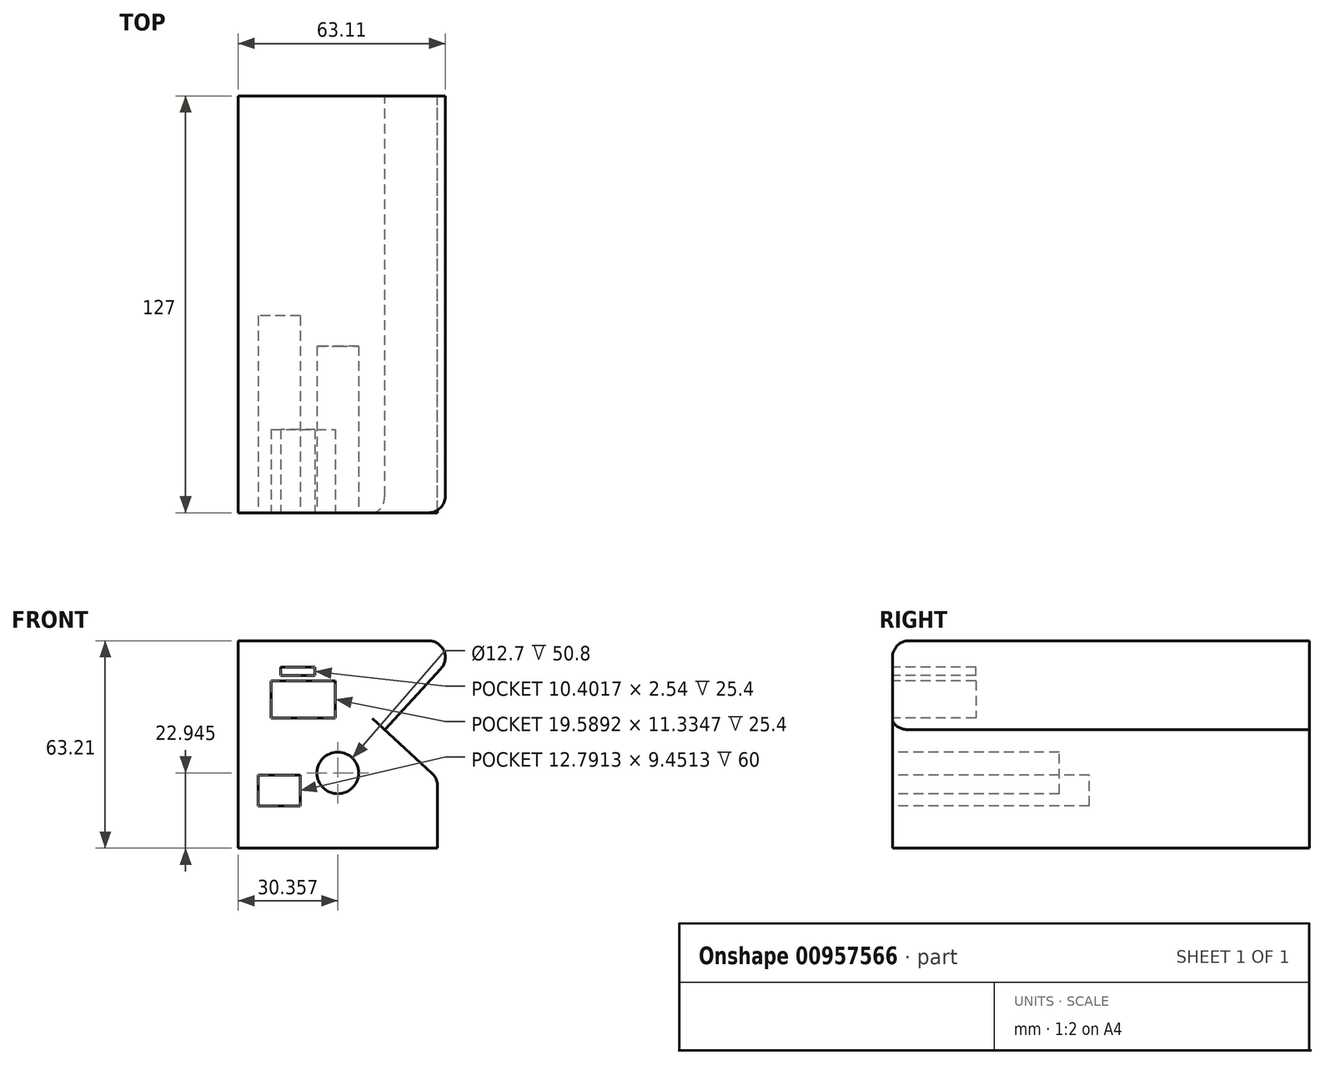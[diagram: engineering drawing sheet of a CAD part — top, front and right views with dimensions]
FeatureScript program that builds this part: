
annotation { "Feature Type Name" : "Feature", "Feature Type Description" : "" }
export const myFeature = defineFeature(function(context is Context, id is Id, definition is map)
    precondition{}
    {
        {
            var Q0;
            Q0=qCreatedBy(makeId("Front.planeOp"),FACE);
            var sketch = newSketch(context, id + "F0", { "sketchPlane" : qUnion([Q0])});
            skLineSegment(sketch, "E0", {"start": v(0, 0) * mm, "end": v(0, 63.21) * mm});
            skLineSegment(sketch, "E1", {"start": v(0, 63.21) * mm, "end": v(69.6, 63.21) * mm});
            skLineSegment(sketch, "E2", {"start": v(69.6, 63.21) * mm, "end": v(44.64, 36.06) * mm});
            skLineSegment(sketch, "E3", {"start": v(44.64, 36.06) * mm, "end": v(60.71, 21.29) * mm});
            skLineSegment(sketch, "E4", {"start": v(60.71, 21.29) * mm, "end": v(60.71, 0) * mm});
            skLineSegment(sketch, "E5", {"start": v(60.71, 0) * mm, "end": v(0, 0) * mm});
            skSolve(sketch);
        }
        {
            var Q0;
            Q0 = qSketchRegion(id + "F0", true);
            extrude(context, id + "F1", {"entities" : qUnion([Q0]), "depth" : 127 * mm, "offsetDistance" : 25.4 * mm});
        }
        {
            var Q0;
            Q0=makeQuery(id+"F1.opExtrude","SWEPT_EDGE",EDGE,{"disambiguationData":[OSD([sQuery(id+"F0.wireOp",EDGE,"E1"),sQuery(id+"F0.wireOp",EDGE,"E2")])]});
            var Q1;
            Q1=makeQuery(id+"F1.opExtrude","SWEPT_EDGE",EDGE,{"disambiguationData":[OSD([sQuery(id+"F0.wireOp",EDGE,"E3"),sQuery(id+"F0.wireOp",EDGE,"E4")])]});
            fillet(context, id + "F2", {"entities" : qUnion([Q0, Q1]), "radius" : 5.08 * mm, "tangentPropagation" : true, "allowEdgeOverflow" : false});
        }
        {
            var Q0;
            Q0=makeQuery(id+"F1.opExtrude","CAP_FACE",FACE,{"disambiguationData":[OSD([sQuery(id+"F0.wireOp",EDGE,"E0"),sQuery(id+"F0.wireOp",EDGE,"E1"),sQuery(id+"F0.wireOp",EDGE,"E2"),sQuery(id+"F0.wireOp",EDGE,"E3"),sQuery(id+"F0.wireOp",EDGE,"E4"),sQuery(id+"F0.wireOp",EDGE,"E5")])],"isStart":false});
            var sketch = newSketch(context, id + "F3", { "sketchPlane" : qUnion([Q0])});
            skCircle(sketch, "E6", {"center": v(30.36, 22.94) * mm, "radius": 6.35 * mm});
            skPoint(sketch, "E6.centerSnap0", {"position": v(30.36, 0) * mm});
            skSolve(sketch);
        }
        {
            var Q0;
            Q0=makeQuery(id+"F3.imprint","IMPRINT",FACE,{"disambiguationData":[TD([[makeQuery(id+"F3.imprint","IMPRINT",EDGE,{"derivedFrom":sQuery(id+"F3.wireOp",EDGE,"E6")}),1.0]])]});
            var Q1;
            Q1=sQuery(id+"F3.wireOp",EDGE,"E6");
            extrude(context, id + "F4", {"entities" : qUnion([Q0]), "operationType" : NewBodyOperationType.REMOVE, "surfaceEntities" : qUnion([Q1]), "oppositeDirection" : true, "depth" : 50.8 * mm, "offsetDistance" : 25.4 * mm});
        }
        {
            var Q0;
            Q0=makeQuery(id+"F1.opExtrude","CAP_FACE",FACE,{"disambiguationData":[OSD([sQuery(id+"F0.wireOp",EDGE,"E0"),sQuery(id+"F0.wireOp",EDGE,"E1"),sQuery(id+"F0.wireOp",EDGE,"E2"),sQuery(id+"F0.wireOp",EDGE,"E3"),sQuery(id+"F0.wireOp",EDGE,"E4"),sQuery(id+"F0.wireOp",EDGE,"E5")])],"isStart":false});
            var sketch = newSketch(context, id + "F5", { "sketchPlane" : qUnion([Q0])});
            skLineSegment(sketch, "E7.bottom", {"start": v(10.05, 51.03) * mm, "end": v(29.64, 51.03) * mm});
            skLineSegment(sketch, "E7.top", {"start": v(10.05, 39.7) * mm, "end": v(29.64, 39.7) * mm});
            skLineSegment(sketch, "E7.left", {"start": v(10.05, 51.03) * mm, "end": v(10.05, 39.7) * mm});
            skLineSegment(sketch, "E7.right", {"start": v(29.64, 51.03) * mm, "end": v(29.64, 39.7) * mm});
            skPoint(sketch, "E7.middle", {"position": v(19.85, 45.37) * mm});
            skSolve(sketch);
        }
        {
            var Q0;
            Q0=makeQuery(id+"F1.opExtrude","CAP_FACE",FACE,{"disambiguationData":[OSD([sQuery(id+"F0.wireOp",EDGE,"E0"),sQuery(id+"F0.wireOp",EDGE,"E1"),sQuery(id+"F0.wireOp",EDGE,"E2"),sQuery(id+"F0.wireOp",EDGE,"E3"),sQuery(id+"F0.wireOp",EDGE,"E4"),sQuery(id+"F0.wireOp",EDGE,"E5")])],"isStart":false});
            var sketch = newSketch(context, id + "F6", { "sketchPlane" : qUnion([Q0])});
            skLineSegment(sketch, "E8.bottom", {"start": v(23.4, 55.13) * mm, "end": v(13, 55.13) * mm});
            skLineSegment(sketch, "E8.top", {"start": v(23.4, 52.59) * mm, "end": v(13, 52.59) * mm});
            skLineSegment(sketch, "E8.left", {"start": v(23.4, 52.59) * mm, "end": v(23.4, 55.13) * mm});
            skLineSegment(sketch, "E8.right", {"start": v(13, 52.59) * mm, "end": v(13, 55.13) * mm});
            skPoint(sketch, "E8.middle", {"position": v(18.2, 53.86) * mm});
            skSolve(sketch);
        }
        {
            var Q0;
            Q0 = qSketchRegion(id + "F6", true);
            extrude(context, id + "F7", {"entities" : qUnion([Q0]), "operationType" : NewBodyOperationType.REMOVE, "oppositeDirection" : true, "depth" : 25.4 * mm, "offsetDistance" : 25.4 * mm});
        }
        {
            var Q0;
            Q0=makeQuery(id+"F5.imprint","IMPRINT",FACE,{"disambiguationData":[TD([[makeQuery(id+"F5.imprint","IMPRINT",EDGE,{"derivedFrom":sQuery(id+"F5.wireOp",EDGE,"E7.bottom")}),-1.0]])]});
            var Q1;
            Q1=sQuery(id+"F5.wireOp",EDGE,"E7.bottom");
            var Q2;
            Q2=sQuery(id+"F5.wireOp",EDGE,"E7.right");
            var Q3;
            Q3=sQuery(id+"F5.wireOp",EDGE,"E7.top");
            var Q4;
            Q4=sQuery(id+"F5.wireOp",EDGE,"E7.left");
            extrude(context, id + "F8", {"entities" : qUnion([Q0]), "operationType" : NewBodyOperationType.REMOVE, "surfaceEntities" : qUnion([Q1, Q2, Q3, Q4]), "oppositeDirection" : true, "depth" : 25.4 * mm, "offsetDistance" : 25.4 * mm});
        }
        {
            var Q0;
            Q0=makeQuery(id+"F1.opExtrude","CAP_EDGE",EDGE,{"disambiguationData":[OSD([sQuery(id+"F0.wireOp",EDGE,"E1")])],"isStart":false});
            fillet(context, id + "F9", {"entities" : qUnion([Q0]), "radius" : 5.08 * mm, "tangentPropagation" : true, "allowEdgeOverflow" : false});
        }
        {
            var Q0;
            Q0=makeQuery(id+"F1.opExtrude","CAP_FACE",FACE,{"disambiguationData":[OSD([sQuery(id+"F0.wireOp",EDGE,"E0"),sQuery(id+"F0.wireOp",EDGE,"E1"),sQuery(id+"F0.wireOp",EDGE,"E2"),sQuery(id+"F0.wireOp",EDGE,"E3"),sQuery(id+"F0.wireOp",EDGE,"E4"),sQuery(id+"F0.wireOp",EDGE,"E5")])],"isStart":false});
            var sketch = newSketch(context, id + "F10", { "sketchPlane" : qUnion([Q0])});
            skLineSegment(sketch, "E9.bottom", {"start": v(18.92, 12.87) * mm, "end": v(6.12, 12.87) * mm});
            skLineSegment(sketch, "E9.top", {"start": v(18.92, 22.32) * mm, "end": v(6.12, 22.32) * mm});
            skLineSegment(sketch, "E9.left", {"start": v(18.92, 12.87) * mm, "end": v(18.92, 22.32) * mm});
            skLineSegment(sketch, "E9.right", {"start": v(6.12, 12.87) * mm, "end": v(6.12, 22.32) * mm});
            skSolve(sketch);
        }
        {
            var Q0;
            Q0 = qSketchRegion(id + "F10", true);
            extrude(context, id + "F11", {"entities" : qUnion([Q0]), "operationType" : NewBodyOperationType.REMOVE, "oppositeDirection" : true, "depth" : 60 * mm, "offsetDistance" : 25.4 * mm});
        }
    });
